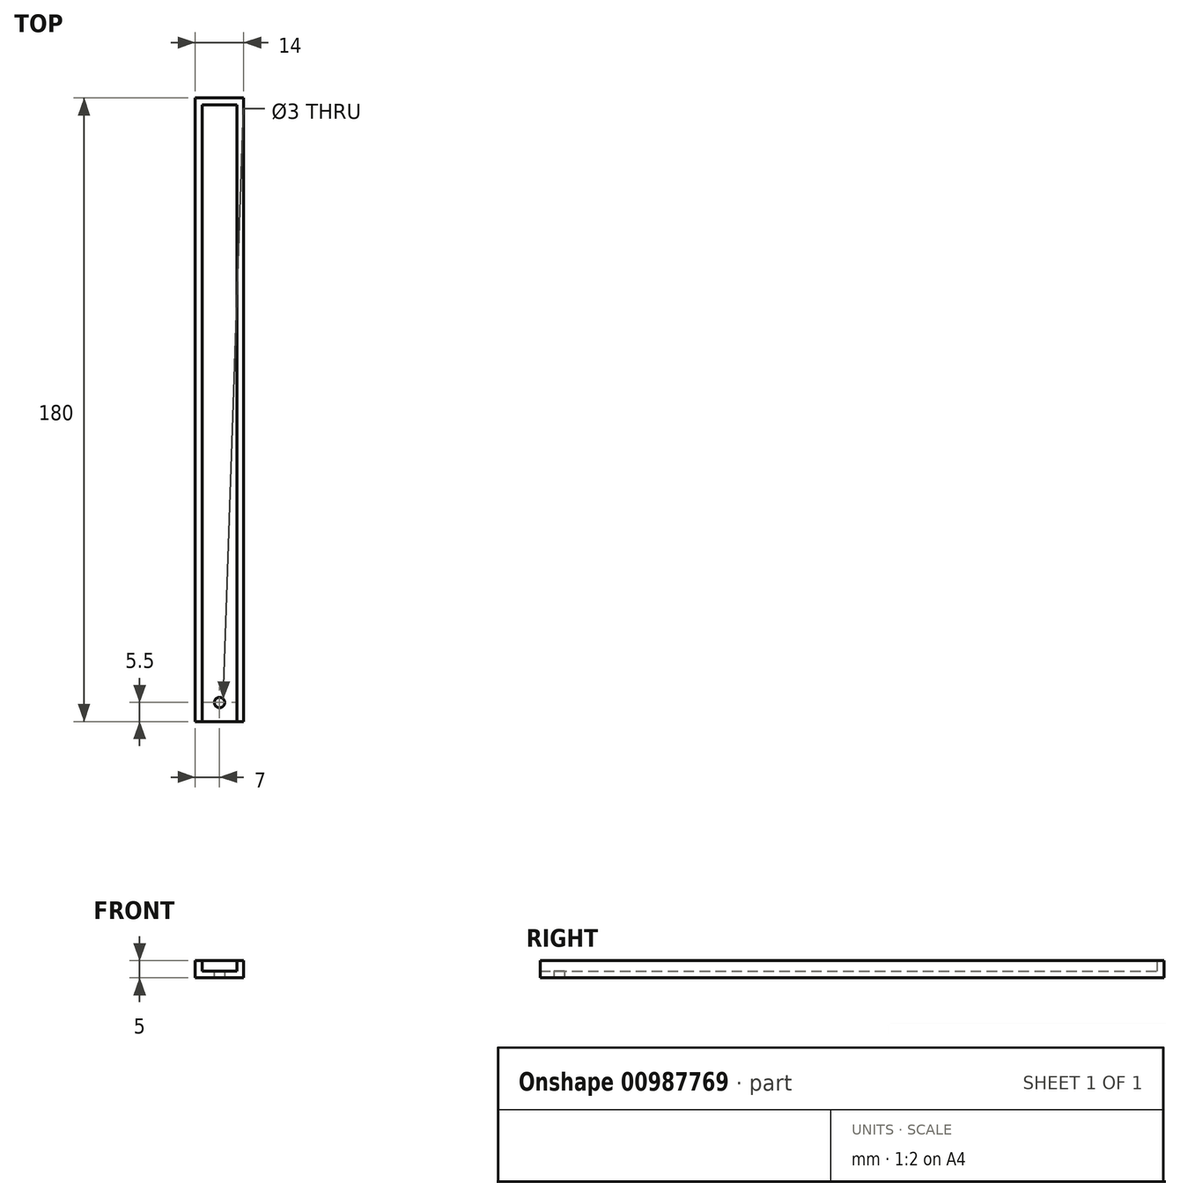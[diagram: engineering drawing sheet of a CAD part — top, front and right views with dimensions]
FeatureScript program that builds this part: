
annotation { "Feature Type Name" : "Feature", "Feature Type Description" : "" }
export const myFeature = defineFeature(function(context is Context, id is Id, definition is map)
    precondition{}
    {
        {
            var Q0;
            Q0=qCreatedBy(makeId("Top.planeOp"),FACE);
            var sketch = newSketch(context, id + "F0", { "sketchPlane" : qUnion([Q0])});
            skLineSegment(sketch, "E0.bottom", {"start": v(-7, 90) * mm, "end": v(7, 90) * mm});
            skLineSegment(sketch, "E0.top", {"start": v(-7, -90) * mm, "end": v(7, -90) * mm});
            skLineSegment(sketch, "E0.left", {"start": v(-7, 90) * mm, "end": v(-7, -90) * mm});
            skLineSegment(sketch, "E0.right", {"start": v(7, 90) * mm, "end": v(7, -90) * mm});
            skPoint(sketch, "E0.middle", {"position": v(0, 0) * mm});
            skLineSegment(sketch, "E1.0", {"start": v(5, 88) * mm, "end": v(5, -90) * mm});
            skLineSegment(sketch, "E1.1", {"start": v(-5, 88) * mm, "end": v(5, 88) * mm});
            skLineSegment(sketch, "E1.2", {"start": v(-5, 88) * mm, "end": v(-5, -90) * mm});
            skLineSegment(sketch, "E2", {"start": v(0, 88) * mm, "end": v(0, -79) * mm});
            skLineSegment(sketch, "E3", {"start": v(7, -79) * mm, "end": v(-7, -79) * mm});
            skLineSegment(sketch, "E4", {"start": v(-5, -90) * mm, "end": v(5, -79) * mm});
            skLineSegment(sketch, "E5", {"start": v(-5, -79) * mm, "end": v(5, -90) * mm});
            skPoint(sketch, "E6", {"position": v(0, -84.5) * mm});
            skCircle(sketch, "E7", {"center": v(0, -84.5) * mm, "radius": 1.5 * mm});
            skSolve(sketch);
        }
        {
            var Q0;
            {var subQ6=sQuery(id+"F0.wireOp",EDGE,"E0.bottom");Q0=makeQuery(id+"F0.imprint","IMPRINT",FACE,{"disambiguationData":[TD([[makeQuery(id+"F0.imprint","IMPRINT",EDGE,{"derivedFrom":subQ6}),-1.0]])]});}
            var Q1;
            {var subQ3=sQuery(id+"F0.wireOp",EDGE,"E2");Q1=makeQuery(id+"F0.imprint","IMPRINT",FACE,{"disambiguationData":[TD([[makeQuery(id+"F0.imprint","IMPRINT",EDGE,{"derivedFrom":subQ3}),-1.0]])]});}
            var Q2;
            {var subQ5=sQuery(id+"F0.wireOp",EDGE,"E2");Q2=makeQuery(id+"F0.imprint","IMPRINT",FACE,{"disambiguationData":[TD([[makeQuery(id+"F0.imprint","IMPRINT",EDGE,{"derivedFrom":subQ5}),1.0]])]});}
            var Q3;
            {var subQ0=sQuery(id+"F0.wireOp",EDGE,"E0.left");var subQ1=sQuery(id+"F0.wireOp",EDGE,"E0.top");var subQ2=makeQuery(id+"F0.imprint","INTERSECT",VERTEX,{"derivedFrom":[subQ1,subQ0]});Q3=makeQuery(id+"F0.imprint","IMPRINT",FACE,{"disambiguationData":[TD([[makeQuery(id+"F0.imprint","IMPRINT",EDGE,{"disambiguationData":[TD([[subQ2,1.0]])],"derivedFrom":subQ0}),1.0]])]});}
            var Q4;
            {var subQ0=sQuery(id+"F0.wireOp",EDGE,"E4");var subQ5=sQuery(id+"F0.wireOp",EDGE,"E7");var subQ7=makeQuery(id+"F0.imprint","INTERSECT",VERTEX,{"disambiguationData":[OD(0.0)],"derivedFrom":[subQ0,subQ5]});Q4=makeQuery(id+"F0.imprint","IMPRINT",FACE,{"disambiguationData":[TD([[makeQuery(id+"F0.imprint","IMPRINT",EDGE,{"disambiguationData":[TD([[subQ7,1.0]])],"derivedFrom":subQ5}),-1.0]])]});}
            var Q5;
            {var subQ3=sQuery(id+"F0.wireOp",EDGE,"E7");var subQ5=sQuery(id+"F0.wireOp",EDGE,"E4");var subQ7=makeQuery(id+"F0.imprint","INTERSECT",VERTEX,{"disambiguationData":[OD(1.0)],"derivedFrom":[subQ5,subQ3]});Q5=makeQuery(id+"F0.imprint","IMPRINT",FACE,{"disambiguationData":[TD([[makeQuery(id+"F0.imprint","IMPRINT",EDGE,{"disambiguationData":[TD([[subQ7,-1.0]])],"derivedFrom":subQ3}),-1.0]])]});}
            var Q6;
            {var subQ3=sQuery(id+"F0.wireOp",EDGE,"E4");var subQ5=sQuery(id+"F0.wireOp",EDGE,"E7");var subQ6=makeQuery(id+"F0.imprint","INTERSECT",VERTEX,{"disambiguationData":[OD(1.0)],"derivedFrom":[subQ3,subQ5]});Q6=makeQuery(id+"F0.imprint","IMPRINT",FACE,{"disambiguationData":[TD([[makeQuery(id+"F0.imprint","IMPRINT",EDGE,{"disambiguationData":[TD([[subQ6,1.0]])],"derivedFrom":subQ5}),-1.0]])]});}
            var Q7;
            {var subQ3=sQuery(id+"F0.wireOp",EDGE,"E4");var subQ5=sQuery(id+"F0.wireOp",EDGE,"E7");var subQ6=makeQuery(id+"F0.imprint","INTERSECT",VERTEX,{"disambiguationData":[OD(0.0)],"derivedFrom":[subQ3,subQ5]});Q7=makeQuery(id+"F0.imprint","IMPRINT",FACE,{"disambiguationData":[TD([[makeQuery(id+"F0.imprint","IMPRINT",EDGE,{"disambiguationData":[TD([[subQ6,-1.0]])],"derivedFrom":subQ5}),-1.0]])]});}
            var Q8;
            {var subQ0=sQuery(id+"F0.wireOp",EDGE,"E0.right");var subQ1=sQuery(id+"F0.wireOp",EDGE,"E0.top");var subQ2=makeQuery(id+"F0.imprint","INTERSECT",VERTEX,{"derivedFrom":[subQ1,subQ0]});Q8=makeQuery(id+"F0.imprint","IMPRINT",FACE,{"disambiguationData":[TD([[makeQuery(id+"F0.imprint","IMPRINT",EDGE,{"disambiguationData":[TD([[subQ2,1.0]])],"derivedFrom":subQ0}),-1.0]])]});}
            extrude(context, id + "F1", {"entities" : qUnion([Q0, Q1, Q2, Q3, Q4, Q5, Q6, Q7, Q8]), "depth" : 2 * mm, "offsetDistance" : 25 * mm});
        }
        {
            var Q0;
            {var subQ6=sQuery(id+"F0.wireOp",EDGE,"E0.bottom");Q0=makeQuery(id+"F0.imprint","IMPRINT",FACE,{"disambiguationData":[TD([[makeQuery(id+"F0.imprint","IMPRINT",EDGE,{"derivedFrom":subQ6}),-1.0]])]});}
            var Q1;
            {var subQ0=sQuery(id+"F0.wireOp",EDGE,"E0.right");var subQ1=sQuery(id+"F0.wireOp",EDGE,"E0.top");var subQ2=makeQuery(id+"F0.imprint","INTERSECT",VERTEX,{"derivedFrom":[subQ1,subQ0]});Q1=makeQuery(id+"F0.imprint","IMPRINT",FACE,{"disambiguationData":[TD([[makeQuery(id+"F0.imprint","IMPRINT",EDGE,{"disambiguationData":[TD([[subQ2,1.0]])],"derivedFrom":subQ0}),-1.0]])]});}
            var Q2;
            {var subQ0=sQuery(id+"F0.wireOp",EDGE,"E0.left");var subQ1=sQuery(id+"F0.wireOp",EDGE,"E0.top");var subQ2=makeQuery(id+"F0.imprint","INTERSECT",VERTEX,{"derivedFrom":[subQ1,subQ0]});Q2=makeQuery(id+"F0.imprint","IMPRINT",FACE,{"disambiguationData":[TD([[makeQuery(id+"F0.imprint","IMPRINT",EDGE,{"disambiguationData":[TD([[subQ2,1.0]])],"derivedFrom":subQ0}),1.0]])]});}
            extrude(context, id + "F2", {"entities" : qUnion([Q0, Q1, Q2]), "operationType" : NewBodyOperationType.ADD, "depth" : 5 * mm, "offsetDistance" : 25 * mm});
        }
    });
